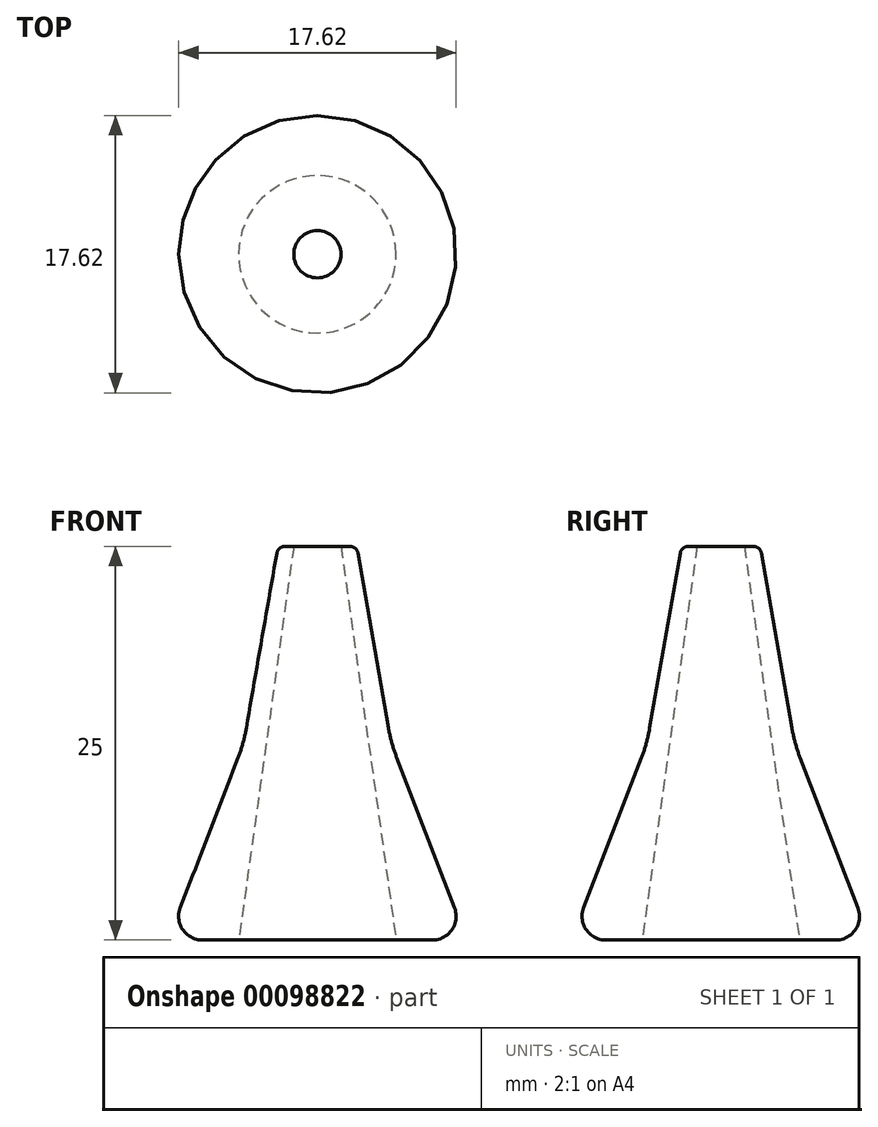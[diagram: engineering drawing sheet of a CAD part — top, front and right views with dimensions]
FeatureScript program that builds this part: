
annotation { "Feature Type Name" : "Feature", "Feature Type Description" : "" }
export const myFeature = defineFeature(function(context is Context, id is Id, definition is map)
    precondition{}
    {
        {
            var Q0;
            Q0=qCreatedBy(makeId("Right.planeOp"),FACE);
            var sketch = newSketch(context, id + "F0", { "sketchPlane" : qUnion([Q0])});
            skLineSegment(sketch, "E0", {"start": v(0, 0) * mm, "end": v(0, 25) * mm});
            skLineSegment(sketch, "E1", {"start": v(0, 0) * mm, "end": v(-9.5, 0) * mm});
            skLineSegment(sketch, "E2", {"start": v(-9.5, 0) * mm, "end": v(-4.68, 12.5) * mm});
            skLineSegment(sketch, "E3", {"start": v(-4.68, 12.5) * mm, "end": v(-2.5, 25) * mm});
            skLineSegment(sketch, "E4", {"start": v(-2.5, 25) * mm, "end": v(0, 25) * mm});
            skSolve(sketch);
        }
        {
            var Q0;
            Q0 = qSketchRegion(id + "F0", true);
            var Q1;
            Q1=sQuery(id+"F0.wireOp",EDGE,"E0");
            revolve(context, id + "F1", {"entities" : qUnion([Q0]), "axis" : qUnion([Q1]), "revolveType" : RevolveType.FULL});
        }
        {
            var Q0;
            Q0=makeQuery(id+"F1.opRevolve","SWEPT_FACE",FACE,{"disambiguationData":[OSD([sQuery(id+"F0.wireOp",EDGE,"E1")])]});
            var sketch = newSketch(context, id + "F2", { "sketchPlane" : qUnion([Q0])});
            skCircle(sketch, "E5", {"center": v(0, 0) * mm, "radius": 5 * mm});
            skSolve(sketch);
        }
        {
            var Q0;
            Q0=makeQuery(id+"F1.opRevolve","SWEPT_FACE",FACE,{"disambiguationData":[OSD([sQuery(id+"F0.wireOp",EDGE,"E4")])]});
            var sketch = newSketch(context, id + "F3", { "sketchPlane" : qUnion([Q0])});
            skCircle(sketch, "E6", {"center": v(0, 0) * mm, "radius": 1.5 * mm});
            skSolve(sketch);
        }
        {
            var Q1;
            Q1=makeQuery(id+"F3.imprint","IMPRINT",FACE,{"disambiguationData":[TD([[makeQuery(id+"F3.imprint","IMPRINT",EDGE,{"derivedFrom":sQuery(id+"F3.wireOp",EDGE,"E6")}),1.0]])]});
            var Q2;
            Q2=makeQuery(id+"F2.imprint","IMPRINT",FACE,{"disambiguationData":[TD([[makeQuery(id+"F2.imprint","IMPRINT",EDGE,{"derivedFrom":sQuery(id+"F2.wireOp",EDGE,"E5")}),1.0]])]});
            loft(context, id + "F4", {"operationType" : NewBodyOperationType.REMOVE, "sheetProfilesArray" : [{ "sheetProfileEntities" : qUnion([Q1]) }, { "sheetProfileEntities" : qUnion([Q2]) }]});
        }
        {
            var Q0;
            Q0=makeQuery(id+"F1.opRevolve","SWEPT_EDGE",EDGE,{"disambiguationData":[OSD([sQuery(id+"F0.wireOp",EDGE,"E1"),sQuery(id+"F0.wireOp",EDGE,"E2")])]});
            fillet(context, id + "F5", {"entities" : qUnion([Q0]), "radius" : 1.5 * mm, "tangentPropagation" : true, "allowEdgeOverflow" : false});
        }
        {
            var Q0;
            Q0=makeQuery(id+"F4.boolean.opBoolean","COPY",EDGE,{"derivedFrom":makeQuery(id+"F4.opLoft","MID_CAP_EDGE",EDGE,{"disambiguationData":[OSD([sQuery(id+"F2.wireOp",EDGE,"E5"),sQuery(id+"F3.wireOp",EDGE,"E6")])],"capPos":1.0})});
            var Q1;
            Q1=makeQuery(id+"F1.opRevolve","SWEPT_EDGE",EDGE,{"disambiguationData":[OSD([sQuery(id+"F0.wireOp",EDGE,"E3"),sQuery(id+"F0.wireOp",EDGE,"E4")])]});
            var Q2;
            Q2=makeQuery(id+"F4.boolean.opBoolean","COPY",EDGE,{"derivedFrom":makeQuery(id+"F4.opLoft","MID_CAP_EDGE",EDGE,{"disambiguationData":[OSD([sQuery(id+"F3.wireOp",EDGE,"E6")])],"capPos":0.0})});
            fillet(context, id + "F6", {"entities" : qUnion([Q0, Q1, Q2]), "radius" : .5 * mm, "tangentPropagation" : true, "allowEdgeOverflow" : false});
        }
        {
            var Q0;
            Q0=makeQuery(id+"F1.opRevolve","SWEPT_EDGE",EDGE,{"disambiguationData":[OSD([sQuery(id+"F0.wireOp",EDGE,"E2"),sQuery(id+"F0.wireOp",EDGE,"E3")])]});
            fillet(context, id + "F7", {"entities" : qUnion([Q0]), "radius" : 10 * mm, "tangentPropagation" : true, "allowEdgeOverflow" : false});
        }
    });
